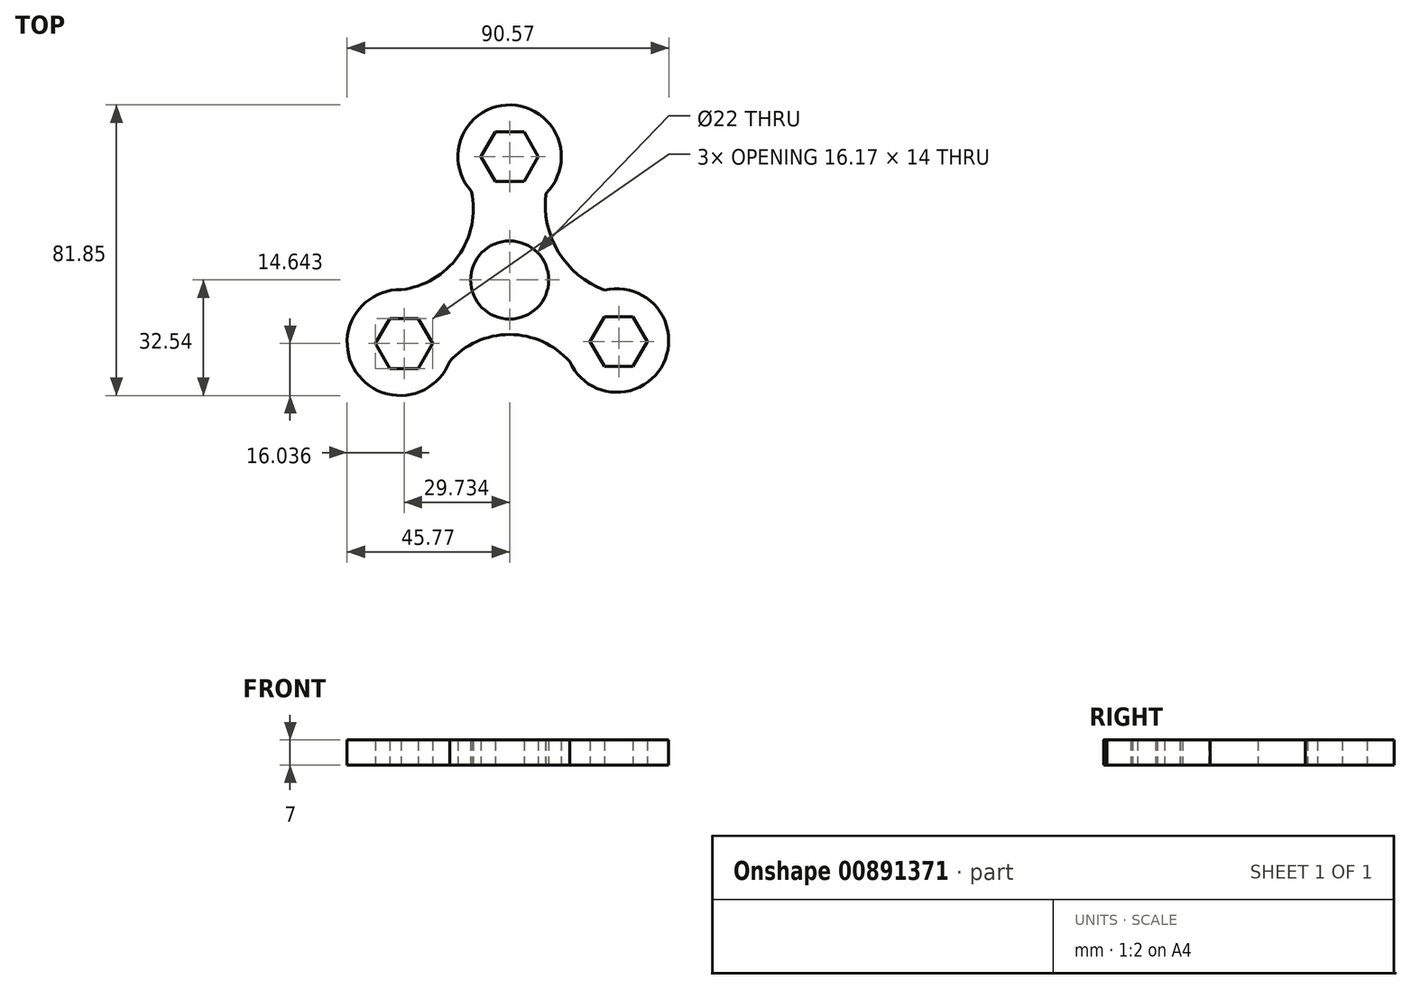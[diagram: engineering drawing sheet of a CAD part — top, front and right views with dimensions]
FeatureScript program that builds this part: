
annotation { "Feature Type Name" : "Feature", "Feature Type Description" : "" }
export const myFeature = defineFeature(function(context is Context, id is Id, definition is map)
    precondition{}
    {
        {
            var Q0;
            Q0=qCreatedBy(makeId("Top.planeOp"),FACE);
            var sketch = newSketch(context, id + "F0", { "sketchPlane" : qUnion([Q0])});
            skCircle(sketch, "E0", {"center": v(0, 0) * mm, "radius": 11 * mm});
            skCircle(sketch, "E1.cCircle", {"center": v(0, 34.74) * mm, "radius": 7 * mm, "construction": true});
            skLineSegment(sketch, "E1.0", {"start": v(4.04, 27.74) * mm, "end": v(-4.04, 27.74) * mm});
            skLineSegment(sketch, "E1.1", {"start": v(-4.04, 27.74) * mm, "end": v(-8.08, 34.74) * mm});
            skLineSegment(sketch, "E1.2", {"start": v(-8.08, 34.74) * mm, "end": v(-4.04, 41.74) * mm});
            skLineSegment(sketch, "E1.3", {"start": v(-4.04, 41.74) * mm, "end": v(4.04, 41.74) * mm});
            skLineSegment(sketch, "E1.4", {"start": v(4.04, 41.74) * mm, "end": v(8.08, 34.74) * mm});
            skLineSegment(sketch, "E1.5", {"start": v(8.08, 34.74) * mm, "end": v(4.04, 27.74) * mm});
            skPoint(sketch, "E1.0.midPoint", {"position": v(0, 27.74) * mm});
            skCircle(sketch, "E2.1.0", {"center": v(-29.73, -17.9) * mm, "radius": 7 * mm, "construction": true});
            skLineSegment(sketch, "E2.1.1", {"start": v(-33.78, -24.9) * mm, "end": v(-37.82, -17.9) * mm});
            skLineSegment(sketch, "E2.1.2", {"start": v(-25.7, -24.9) * mm, "end": v(-33.78, -24.9) * mm});
            skLineSegment(sketch, "E2.1.3", {"start": v(-21.65, -17.9) * mm, "end": v(-25.7, -24.9) * mm});
            skLineSegment(sketch, "E2.1.4", {"start": v(-25.7, -10.9) * mm, "end": v(-21.65, -17.9) * mm});
            skLineSegment(sketch, "E2.1.5", {"start": v(-33.78, -10.9) * mm, "end": v(-25.7, -10.9) * mm});
            skLineSegment(sketch, "E2.1.6", {"start": v(-37.82, -17.9) * mm, "end": v(-33.78, -10.9) * mm});
            skCircle(sketch, "E2.2.0", {"center": v(30.72, -17.33) * mm, "radius": 7 * mm, "construction": true});
            skLineSegment(sketch, "E2.2.1", {"start": v(38.8, -17.33) * mm, "end": v(34.76, -24.33) * mm});
            skLineSegment(sketch, "E2.2.2", {"start": v(34.76, -10.33) * mm, "end": v(38.8, -17.33) * mm});
            skLineSegment(sketch, "E2.2.3", {"start": v(26.68, -10.33) * mm, "end": v(34.76, -10.33) * mm});
            skLineSegment(sketch, "E2.2.4", {"start": v(22.64, -17.33) * mm, "end": v(26.68, -10.33) * mm});
            skLineSegment(sketch, "E2.2.5", {"start": v(26.68, -24.33) * mm, "end": v(22.64, -17.33) * mm});
            skLineSegment(sketch, "E2.2.6", {"start": v(34.76, -24.33) * mm, "end": v(26.68, -24.33) * mm});
            skPoint(sketch, "E2.center", {"position": v(0.33, -0.16) * mm});
            skPoint(sketch, "E3.center", {"position": v(-1.56, 0.53) * mm});
            skPoint(sketch, "E4.center", {"position": v(11.75, -1.76) * mm});
            skArc(sketch, "E5", {"start": v(10.2, 24.34) * mm, "mid": v(0.39, 49.3) * mm, "end": v(-10.73, 24.9) * mm});
            skArc(sketch, "E6.1.0", {"start": v(-30.55, -2.71) * mm, "mid": v(-43.22, -25.95) * mm, "end": v(-16.92, -22.96) * mm});
            skArc(sketch, "E6.2.0", {"start": v(16.88, -22.96) * mm, "mid": v(43.3, -23.47) * mm, "end": v(26.75, -2.86) * mm});
            skArc(sketch, "E7", {"start": v(-30.55, -2.71) * mm, "mid": v(-14.52, 6.7) * mm, "end": v(-10.73, 24.9) * mm});
            skArc(sketch, "E8", {"start": v(10.2, 24.34) * mm, "mid": v(13.76, 7.87) * mm, "end": v(26.75, -2.86) * mm});
            skArc(sketch, "E9", {"start": v(16.88, -22.96) * mm, "mid": v(-0.02, -15.35) * mm, "end": v(-16.92, -22.96) * mm});
            skSolve(sketch);
        }
        {
            var Q0;
            Q0=makeQuery(id+"F0.imprint","IMPRINT",FACE,{"disambiguationData":[TD([[makeQuery(id+"F0.imprint","IMPRINT",EDGE,{"derivedFrom":sQuery(id+"F0.wireOp",EDGE,"E0")}),-1.0]])]});
            extrude(context, id + "F1", {"entities" : qUnion([Q0]), "depth" : 7 * mm, "offsetDistance" : 25 * mm});
        }
    });
